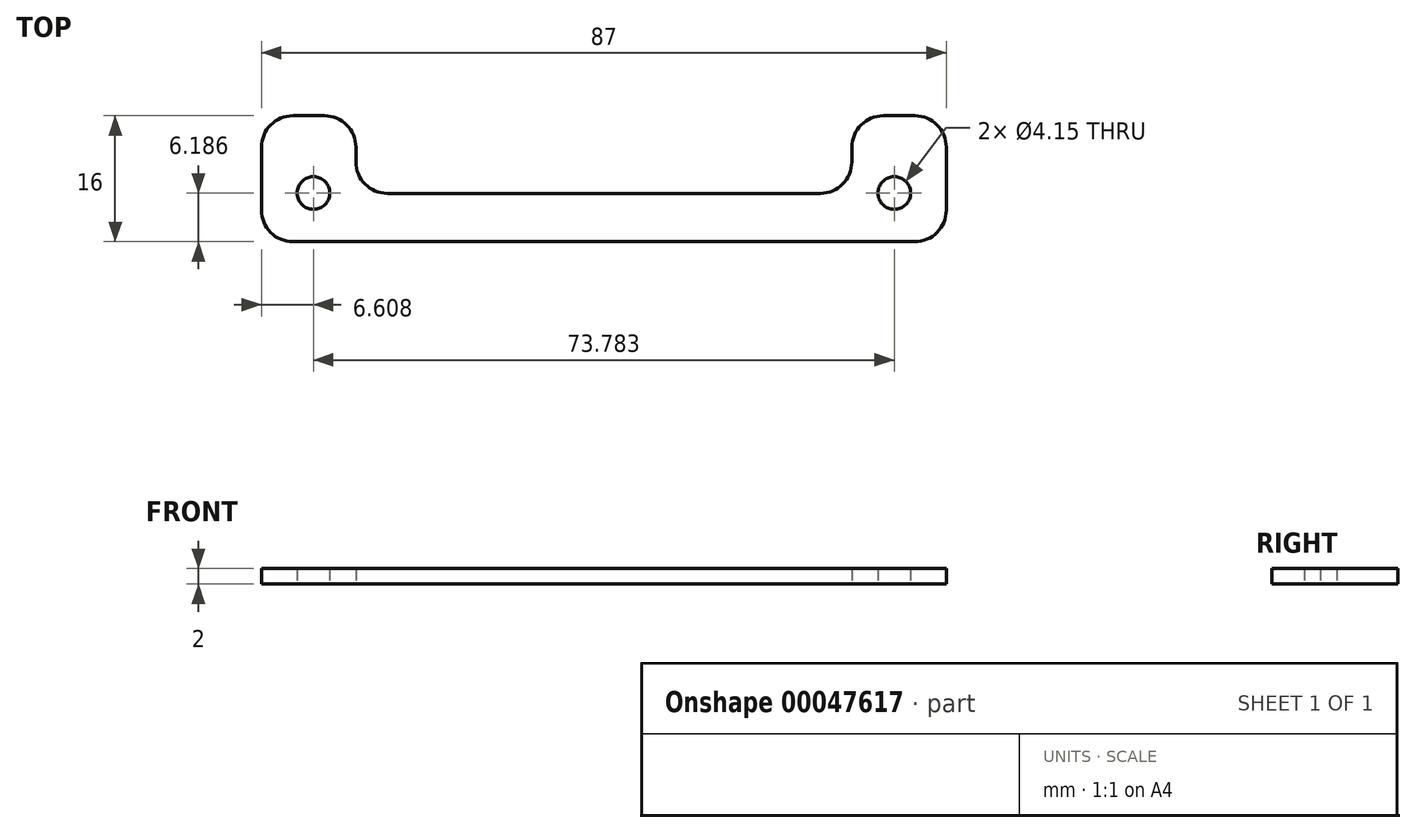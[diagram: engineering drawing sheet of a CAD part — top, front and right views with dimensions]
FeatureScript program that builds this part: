
annotation { "Feature Type Name" : "Feature", "Feature Type Description" : "" }
export const myFeature = defineFeature(function(context is Context, id is Id, definition is map)
    precondition{}
    {
        {
            var Q0;
            Q0=qCreatedBy(makeId("Top.planeOp"),FACE);
            var sketch = newSketch(context, id + "F0", { "sketchPlane" : qUnion([Q0])});
            skLineSegment(sketch, "E0.bottom", {"start": v(39.5, -9.53) * mm, "end": v(-39.5, -9.53) * mm});
            skLineSegment(sketch, "E0.top", {"start": v(39.5, 6.47) * mm, "end": v(35.5, 6.47) * mm});
            skLineSegment(sketch, "E0.left", {"start": v(43.5, -5.53) * mm, "end": v(43.5, 2.46) * mm});
            skLineSegment(sketch, "E0.right", {"start": v(-43.5, -5.54) * mm, "end": v(-43.5, 2.46) * mm});
            skLineSegment(sketch, "E1", {"start": v(-31.5, 2.46) * mm, "end": v(-31.5, 0.6) * mm});
            skLineSegment(sketch, "E2", {"start": v(-27.5, -3.4) * mm, "end": v(27.5, -3.4) * mm});
            skLineSegment(sketch, "E3", {"start": v(31.5, 0.6) * mm, "end": v(31.5, 2.46) * mm});
            skLineSegment(sketch, "E4", {"start": v(0, -3.4) * mm, "end": v(0, -9.53) * mm, "construction": true});
            skLineSegment(sketch, "E5.trimOffspring", {"start": v(-35.5, 6.46) * mm, "end": v(-39.5, 6.46) * mm});
            skPoint(sketch, "E6.orphan", {"position": v(0, 6.46) * mm});
            skPoint(sketch, "E7.visualSharp", {"position": v(-31.5, -3.4) * mm});
            skArc(sketch, "E7.filletArc", {"start": v(-31.5, 0.6) * mm, "mid": v(-30.33, -2.22) * mm, "end": v(-27.5, -3.4) * mm});
            skPoint(sketch, "E8.visualSharp", {"position": v(31.5, -3.4) * mm});
            skArc(sketch, "E8.filletArc", {"start": v(27.5, -3.4) * mm, "mid": v(30.33, -2.22) * mm, "end": v(31.5, 0.6) * mm});
            skPoint(sketch, "E9.visualSharp", {"position": v(-31.5, 6.46) * mm});
            skArc(sketch, "E9.filletArc", {"start": v(-31.5, 2.46) * mm, "mid": v(-32.67, 5.3) * mm, "end": v(-35.5, 6.46) * mm});
            skPoint(sketch, "E10.visualSharp", {"position": v(-43.5, 6.46) * mm});
            skArc(sketch, "E10.filletArc", {"start": v(-39.5, 6.46) * mm, "mid": v(-42.33, 5.3) * mm, "end": v(-43.5, 2.46) * mm});
            skPoint(sketch, "E11.visualSharp", {"position": v(-43.5, -9.53) * mm});
            skArc(sketch, "E11.filletArc", {"start": v(-43.5, -5.54) * mm, "mid": v(-42.33, -8.36) * mm, "end": v(-39.5, -9.54) * mm});
            skPoint(sketch, "E12.visualSharp", {"position": v(43.5, -9.53) * mm});
            skArc(sketch, "E12.filletArc", {"start": v(39.5, -9.53) * mm, "mid": v(42.33, -8.36) * mm, "end": v(43.5, -5.53) * mm});
            skPoint(sketch, "E13.visualSharp", {"position": v(43.5, 6.47) * mm});
            skArc(sketch, "E13.filletArc", {"start": v(43.5, 2.46) * mm, "mid": v(42.33, 5.3) * mm, "end": v(39.5, 6.46) * mm});
            skPoint(sketch, "E14.visualSharp", {"position": v(31.5, 6.47) * mm});
            skArc(sketch, "E14.filletArc", {"start": v(35.5, 6.46) * mm, "mid": v(32.67, 5.3) * mm, "end": v(31.5, 2.46) * mm});
            skLineSegment(sketch, "E15", {"start": v(-43.5, -3.35) * mm, "end": v(43.5, -3.4) * mm, "construction": true});
            skCircle(sketch, "E16", {"center": v(-36.9, -3.35) * mm, "radius": 2.07 * mm});
            skCircle(sketch, "E17.MirrorC", {"center": v(36.9, -3.35) * mm, "radius": 2.07 * mm});
            skSolve(sketch);
        }
        {
            var Q0;
            Q0=makeQuery(id+"F0.imprint","IMPRINT",FACE,{"disambiguationData":[TD([[makeQuery(id+"F0.imprint","IMPRINT",EDGE,{"derivedFrom":sQuery(id+"F0.wireOp",EDGE,"E0.bottom")}),-1.0]])]});
            extrude(context, id + "F1", {"entities" : qUnion([Q0]), "depth" : 2 * mm});
        }
    });
